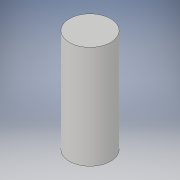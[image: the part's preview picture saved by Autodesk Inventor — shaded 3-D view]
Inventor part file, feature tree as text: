
AUTODESK INVENTOR PART (.ipt)
format: ipt  version: 2019 (Build 230136000, 136)  size: 206,848 bytes
history: native  units: mm
features: extrude x1, sketch x1
ambient origin geometry x8: Origin, YZ Plane, XZ Plane, XY Plane, X Axis, Y Axis, Z Axis, Center Point
bodies: Solid1 (feature_tree)
feature tree (2):
  extrude  "Extrusion1"  Depth=20.0mm TaperAngle=0.0deg
  sketch  "Sketch1"  dims[d0=8.0mm d1=20.0mm d2=0.0mm]
